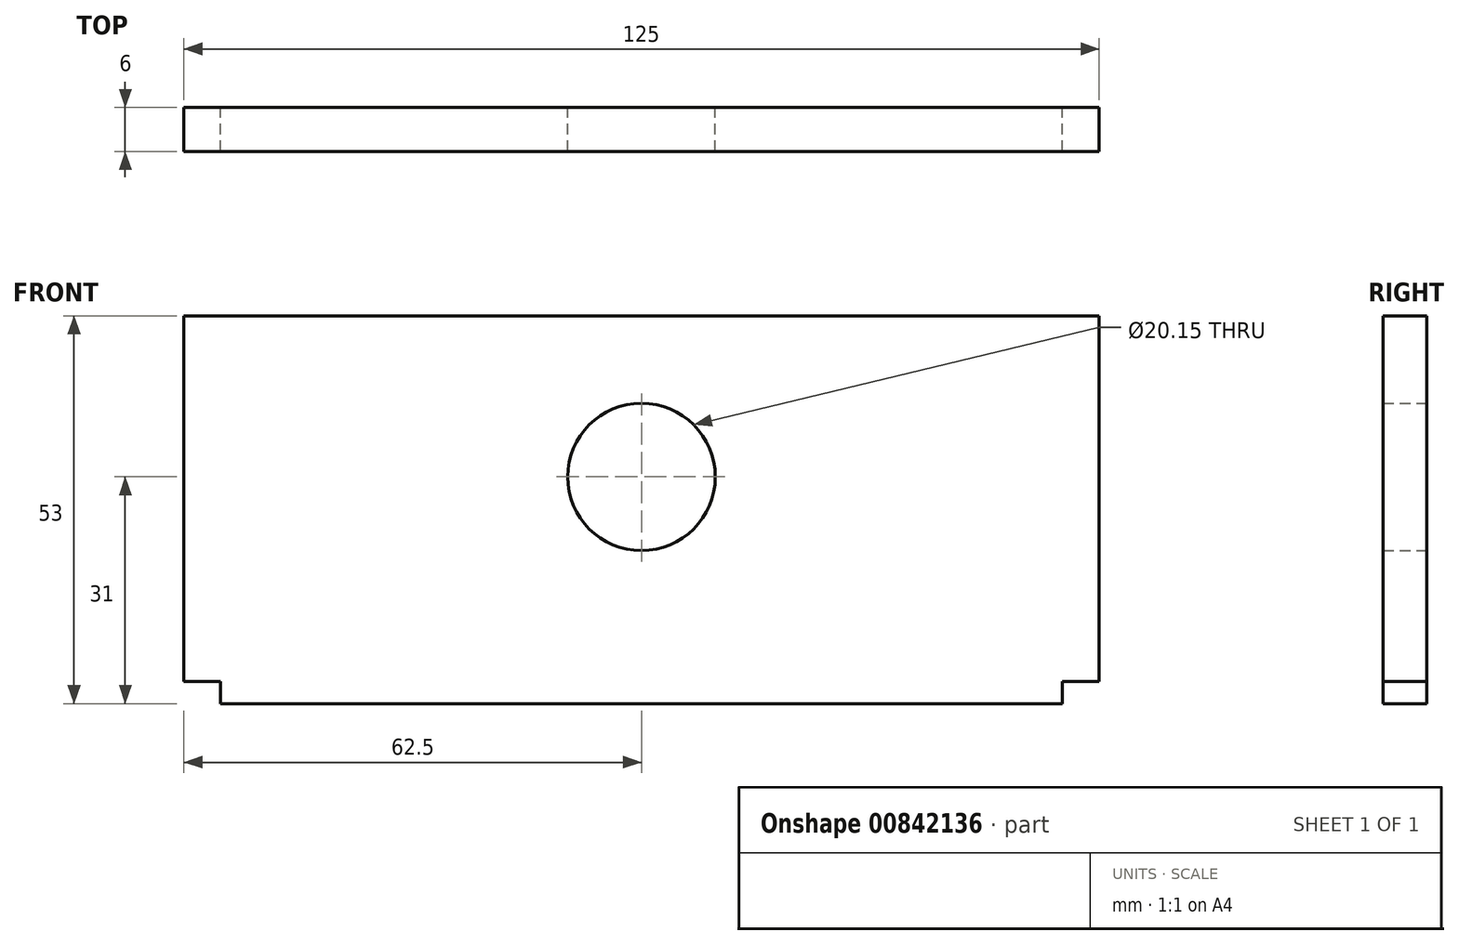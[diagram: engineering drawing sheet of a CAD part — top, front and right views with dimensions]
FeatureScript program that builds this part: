
annotation { "Feature Type Name" : "Feature", "Feature Type Description" : "" }
export const myFeature = defineFeature(function(context is Context, id is Id, definition is map)
    precondition{}
    {
        {
            var Q0;
            Q0=qCreatedBy(makeId("Front.planeOp"),FACE);
            var sketch = newSketch(context, id + "F0", { "sketchPlane" : qUnion([Q0])});
            skLineSegment(sketch, "E0", {"start": v(0, 0) * mm, "end": v(-57.5, 0) * mm});
            skLineSegment(sketch, "E1", {"start": v(-57.5, 0) * mm, "end": v(-57.5, 3) * mm});
            skLineSegment(sketch, "E2", {"start": v(-57.5, 3) * mm, "end": v(-62.5, 3) * mm});
            skLineSegment(sketch, "E3", {"start": v(-62.5, 3) * mm, "end": v(-62.5, 53) * mm});
            skLineSegment(sketch, "E4", {"start": v(-62.5, 53) * mm, "end": v(0, 53) * mm});
            skLineSegment(sketch, "E5", {"start": v(0, 53) * mm, "end": v(0, 41.08) * mm});
            skArc(sketch, "E6", {"start": v(0, 41.08) * mm, "mid": v(-10.07, 31) * mm, "end": v(0, 20.93) * mm});
            skLineSegment(sketch, "E7.trimOffspring", {"start": v(0, 20.93) * mm, "end": v(0, 0) * mm});
            skSolve(sketch);
        }
        {
            var Q0;
            Q0=makeQuery(id+"F0.imprint","IMPRINT",FACE,{"disambiguationData":[TD([[makeQuery(id+"F0.imprint","IMPRINT",EDGE,{"derivedFrom":sQuery(id+"F0.wireOp",EDGE,"E0")}),-1.0]])]});
            extrude(context, id + "F1", {"entities" : qUnion([Q0]), "depth" : 6 * mm, "offsetDistance" : 25 * mm});
        }
        {
            var Q0;
            Q0=makeQuery(id+"F1.opExtrude","SWEPT_BODY",BODY,{"disambiguationData":[OSD([sQuery(id+"F0.wireOp",EDGE,"E0"),sQuery(id+"F0.wireOp",EDGE,"E1"),sQuery(id+"F0.wireOp",EDGE,"E2"),sQuery(id+"F0.wireOp",EDGE,"E3"),sQuery(id+"F0.wireOp",EDGE,"E4"),sQuery(id+"F0.wireOp",EDGE,"E5"),sQuery(id+"F0.wireOp",EDGE,"E6"),sQuery(id+"F0.wireOp",EDGE,"E7.trimOffspring")])]});
            var Q1;
            Q1=makeQuery(id+"F1.opExtrude","SWEPT_FACE",FACE,{"disambiguationData":[OSD([sQuery(id+"F0.wireOp",EDGE,"E5")])]});
            mirror(context, id + "F2", {"operationType" : NewBodyOperationType.ADD, "entities" : qUnion([Q0]), "mirrorPlane" : qUnion([Q1])});
        }
    });
